# Revit family: result
name_source: partatom
category: Plumbing Fixtures
revit_build: Autodesk Revit 2015 (Build: 20140903_1530(x64)
units: mm (PartAtom-declared; Revit-internal decimal feet)

## types (1)
- Default
    BIMobject category = Taps & Mixers
    BIMobject category code = sanitary-taps-mixers
    BIMobject main category = Sanitary
    BIMobject main category code = sanitary
    Brand url = http://www.duravit.com
    Edition number = 1
    GTIN code = https://4063382162946
    IFC Classification = Sanitary Terminal
    Manufacturer name = DURAVIT
    Masterformat 2014 Code = 22 41 39
    Masterformat 2014 Description = Residential Faucets, Supplies, and Trim
    NBS Reference Code = 35-79-95
    NBS Reference Description = Wash Basin And Trough Water Supply Fittings
    OmniClass Code = 23-31 11 00
    OmniClass Description = Faucets
    Product Guid = 2c75101d-747b-417e-8ffa-ac427cb40585
    Product SKU = d-neo-single-lever-shower-mixer-for-concealed-installation-de4210
    Product data url = https://bimobject.com
    Product family = D-Neo
    Product group = Single lever shower mixer for concealed installation
    Product name = DE4210 D-Neo Single lever shower mixer for concealed installation
    Product url = https://duravit-public-assets.s3.eu-central-1.amazonaws.com
    QR code = http://bimobject.com
    Technical description = https://duravit-public-assets.s3.eu-central-1.amazonaws.com
    UNSPSC Code = 301815
    Uniclass 1.4 Code = L72511
    Uniclass 1.4 Description = Taps
    Uniclass 2.0 Code = PR-35-79-95
    Uniclass 2.0 Description = Wash Basin And Trough Water Supply Fittings
    Uniclass 2015 Code = Pr_40_20_87
    Uniclass 2015 Name = Taps and water supply outlet fittings
    Uniformat II Code = D2010
    Uniformat II Description = Plumbing Fixtures

## geometry (parser evidence)
native form markers: Sweep x4
no freeform markers — native parametric forms only
